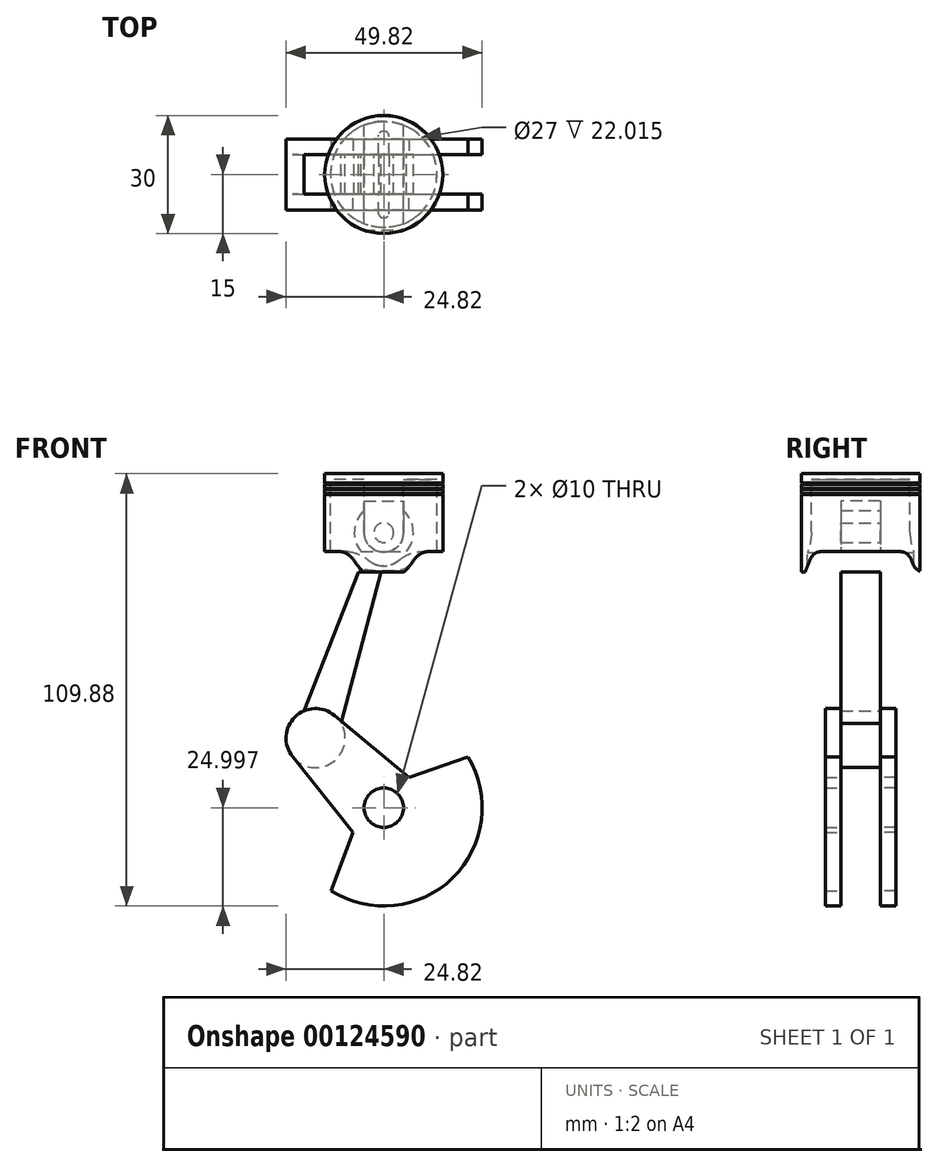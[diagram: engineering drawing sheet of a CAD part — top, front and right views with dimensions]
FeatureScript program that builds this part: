
annotation { "Feature Type Name" : "Feature", "Feature Type Description" : "" }
export const myFeature = defineFeature(function(context is Context, id is Id, definition is map)
    precondition{}
    {
        {
            var Q0;
            Q0=qCreatedBy(makeId("Front.planeOp"),FACE);
            var sketch = newSketch(context, id + "F0", { "sketchPlane" : qUnion([Q0])});
            skLineSegment(sketch, "E0", {"start": v(-89.18, 0) * mm, "end": v(136.85, 0) * mm, "construction": true});
            skLineSegment(sketch, "E1", {"start": v(-89.18, 90) * mm, "end": v(136.85, 90) * mm, "construction": true});
            skLineSegment(sketch, "E2", {"start": v(0, -43.94) * mm, "end": v(0, 141.42) * mm, "construction": true});
            skLineSegment(sketch, "E3", {"start": v(-89.18, 50) * mm, "end": v(92.22, 50) * mm, "construction": true});
            skLineSegment(sketch, "E4", {"start": v(0, 0) * mm, "end": v(-17.32, 10) * mm});
            skLineSegment(sketch, "E5.bottom", {"start": v(-15, 77.2) * mm, "end": v(15, 77.2) * mm});
            skLineSegment(sketch, "E5.top", {"start": v(-15, 52.2) * mm, "end": v(15, 52.2) * mm});
            skLineSegment(sketch, "E5.left", {"start": v(-15, 77.2) * mm, "end": v(-15, 52.2) * mm});
            skLineSegment(sketch, "E5.right", {"start": v(15, 77.2) * mm, "end": v(15, 52.2) * mm});
            skCircle(sketch, "E6", {"center": v(0, 62.2) * mm, "radius": 2.5 * mm});
            skLineSegment(sketch, "E7", {"start": v(-5, 77.2) * mm, "end": v(-5, 62.2) * mm});
            skLineSegment(sketch, "E8", {"start": v(5, 77.2) * mm, "end": v(5, 62.2) * mm});
            skArc(sketch, "E9", {"start": v(-5, 62.2) * mm, "mid": v(0, 57.2) * mm, "end": v(5, 62.2) * mm});
            skLineSegment(sketch, "E10", {"start": v(-5, 70.2) * mm, "end": v(5, 70.2) * mm});
            skLineSegment(sketch, "E11", {"start": v(0, 62.2) * mm, "end": v(-17.32, 10) * mm});
            skSolve(sketch);
        }
        {
            var Q0;
            Q0=qCreatedBy(makeId("Front.planeOp"),FACE);
            var sketch = newSketch(context, id + "F1", { "sketchPlane" : qUnion([Q0])});
            skLineSegment(sketch, "E12.0", {"start": v(0, 77.2) * mm, "end": v(15, 77.2) * mm});
            skLineSegment(sketch, "E12.1", {"start": v(15, 77.2) * mm, "end": v(15, 52.2) * mm});
            skLineSegment(sketch, "E12.2", {"start": v(0, 52.2) * mm, "end": v(15, 52.2) * mm});
            skLineSegment(sketch, "E13", {"start": v(0, 77.2) * mm, "end": v(0, 52.2) * mm});
            skPoint(sketch, "E14.orphan", {"position": v(-15, 77.2) * mm});
            skPoint(sketch, "E15.orphan", {"position": v(-15, 52.2) * mm});
            skSolve(sketch);
        }
        {
            var Q0;
            Q0=makeQuery(id+"F1.imprint","IMPRINT",FACE,{"disambiguationData":[TD([[makeQuery(id+"F1.imprint","IMPRINT",EDGE,{"derivedFrom":sQuery(id+"F1.wireOp",EDGE,"E12.0")}),-1.0]])]});
            var Q1;
            Q1=sQuery(id+"F1.wireOp",EDGE,"E13");
            revolve(context, id + "F2", {"entities" : qUnion([Q0]), "axis" : qUnion([Q1]), "revolveType" : RevolveType.FULL});
        }
        {
            var Q0;
            Q0=makeQuery(id+"F2.opRevolve","SWEPT_FACE",FACE,{"disambiguationData":[OSD([sQuery(id+"F1.wireOp",EDGE,"E12.2")])]});
            shell(context, id + "F3", {"entities" : qUnion([Q0]), "thickness" : 1.5 * mm});
        }
        {
            var Q0;
            {var subQ5=sQuery(id+"F0.wireOp",EDGE,"E10");Q0=makeQuery(id+"F0.imprint","IMPRINT",FACE,{"disambiguationData":[TD([[makeQuery(id+"F0.imprint","IMPRINT",EDGE,{"derivedFrom":subQ5}),1.0]])]});}
            var Q1;
            Q1=makeQuery(id+"F0.imprint","IMPRINT",FACE,{"disambiguationData":[TD([[makeQuery(id+"F0.imprint","IMPRINT",EDGE,{"derivedFrom":sQuery(id+"F0.wireOp",EDGE,"E6")}),-1.0]])]});
            var Q2;
            Q2=makeQuery(id+"F2.opRevolve","SWEPT_FACE",FACE,{"disambiguationData":[OSD([sQuery(id+"F1.wireOp",EDGE,"E12.1")])]});
            var Q3;
            Q3=makeQuery(id+"F3.opShell","OFFSET_FACE",FACE,{"disambiguationData":[OSD([sQuery(id+"F1.wireOp",EDGE,"E12.1")])]});
            extrude(context, id + "F4", {"entities" : qUnion([Q0, Q1]), "operationType" : NewBodyOperationType.ADD, "endBound" : BoundingType.UP_TO_SURFACE, "endBoundEntityFace" : qUnion([Q2]), "depth" : 25 * mm, "hasSecondDirection" : true, "secondDirectionBound" : SecondDirectionBoundingType.UP_TO_SURFACE, "secondDirectionOppositeDirection" : true, "secondDirectionBoundEntityFace" : qUnion([Q3]), "secondDirectionDepth" : 25 * mm});
        }
        {
            var Q0;
            Q0=qCreatedBy(makeId("Front.planeOp"),FACE);
            var sketch = newSketch(context, id + "F5", { "sketchPlane" : qUnion([Q0])});
            skCircle(sketch, "E16", {"center": v(0, 62.2) * mm, "radius": 7.5 * mm});
            skCircle(sketch, "E17", {"center": v(-17.32, 10) * mm, "radius": 4 * mm});
            skCircle(sketch, "E18", {"center": v(-17.32, 10) * mm, "radius": 7.5 * mm});
            skLineSegment(sketch, "E19", {"start": v(0, 54.7) * mm, "end": v(-10.81, 13.73) * mm});
            skLineSegment(sketch, "E20", {"start": v(-4.71, 56.37) * mm, "end": v(-20.3, 16.88) * mm});
            skCircle(sketch, "E21", {"center": v(0, 62.2) * mm, "radius": 2.5 * mm});
            skSolve(sketch);
        }
        {
            var Q0;
            Q0 = qSketchRegion(id + "F5", true);
            extrude(context, id + "F6", {"entities" : qUnion([Q0]), "endBound" : BoundingType.SYMMETRIC, "depth" : 10 * mm});
        }
        {
            var Q0;
            Q0=makeQuery(id+"F6.opExtrude","CAP_FACE",FACE,{"disambiguationData":[OSD([sQuery(id+"F5.wireOp",EDGE,"E16"),sQuery(id+"F5.wireOp",EDGE,"E17"),sQuery(id+"F5.wireOp",EDGE,"E18"),sQuery(id+"F5.wireOp",EDGE,"E19"),sQuery(id+"F5.wireOp",EDGE,"E20"),sQuery(id+"F5.wireOp",EDGE,"E21")])],"isStart":false});
            var sketch = newSketch(context, id + "F7", { "sketchPlane" : qUnion([Q0])});
            skCircle(sketch, "E22.0", {"center": v(-17.32, 10) * mm, "radius": 7.5 * mm});
            skPoint(sketch, "E22.1", {"position": v(-17.32, 10) * mm});
            skCircle(sketch, "E23", {"center": v(0, -7.68) * mm, "radius": 5 * mm});
            skCircle(sketch, "E24", {"center": v(0, -7.68) * mm, "radius": 10 * mm});
            skLineSegment(sketch, "E25", {"start": v(-7.81, -13.92) * mm, "end": v(-23.18, 5.32) * mm});
            skLineSegment(sketch, "E26", {"start": v(-12.52, 15.76) * mm, "end": v(6.4, 0) * mm});
            skLineSegment(sketch, "E27", {"start": v(-7.81, -13.92) * mm, "end": v(0, -7.68) * mm, "construction": true});
            skLineSegment(sketch, "E28", {"start": v(0, -7.68) * mm, "end": v(6.4, 0) * mm, "construction": true});
            skLineSegment(sketch, "E29", {"start": v(0, -7.68) * mm, "end": v(19.26, -27.34) * mm, "construction": true});
            skLineSegment(sketch, "E30", {"start": v(6.4, 0) * mm, "end": v(21.38, 5.28) * mm});
            skLineSegment(sketch, "E31", {"start": v(-7.81, -13.92) * mm, "end": v(-13.4, -28.79) * mm});
            skArc(sketch, "E32", {"start": v(-13.4, -28.79) * mm, "mid": v(17.5, -25.54) * mm, "end": v(21.38, 5.28) * mm});
            skCircle(sketch, "E33.1", {"center": v(-17.32, 10) * mm, "radius": 4 * mm});
            skSolve(sketch);
        }
        {
            var Q0;
            Q0=makeQuery(id+"F5.imprint","IMPRINT",FACE,{"disambiguationData":[TD([[makeQuery(id+"F5.imprint","IMPRINT",EDGE,{"derivedFrom":sQuery(id+"F5.wireOp",EDGE,"E21")}),1.0]])]});
            var Q1;
            Q1=makeQuery(id+"F0.imprint","IMPRINT",FACE,{"disambiguationData":[TD([[makeQuery(id+"F0.imprint","IMPRINT",EDGE,{"derivedFrom":sQuery(id+"F0.wireOp",EDGE,"E6")}),-1.0]])]});
            extrude(context, id + "F8", {"entities" : qUnion([Q0, Q1]), "operationType" : NewBodyOperationType.REMOVE, "endBound" : BoundingType.SYMMETRIC, "oppositeDirection" : true, "depth" : 10 * mm});
        }
        {
            var Q0;
            Q0=qCreatedBy(makeId("Right.planeOp"),FACE);
            var sketch = newSketch(context, id + "F9", { "sketchPlane" : qUnion([Q0])});
            skLineSegment(sketch, "E34", {"start": v(-14.08, 52.2) * mm, "end": v(-12.07, 57.37) * mm});
            skLineSegment(sketch, "E35", {"start": v(-12.07, 57.37) * mm, "end": v(12.07, 57.37) * mm});
            skLineSegment(sketch, "E36", {"start": v(12.07, 57.37) * mm, "end": v(14.08, 52.2) * mm});
            skLineSegment(sketch, "E37", {"start": v(0, -1.25) * mm, "end": v(0, 76.4) * mm, "construction": true});
            skLineSegment(sketch, "E38", {"start": v(-14.08, 52.2) * mm, "end": v(14.08, 52.2) * mm});
            skLineSegment(sketch, "E39.0", {"start": v(-15, 52.2) * mm, "end": v(15, 52.2) * mm});
            skSolve(sketch);
        }
        {
            var Q0;
            Q0 = qSketchRegion(id + "F7", true);
            var Q1;
            Q1=makeQuery(id+"F7.imprint","IMPRINT",FACE,{"disambiguationData":[TD([[makeQuery(id+"F7.imprint","IMPRINT",EDGE,{"derivedFrom":sQuery(id+"F7.wireOp",EDGE,"E33.1")}),1.0]])]});
            extrude(context, id + "F10", {"entities" : qUnion([Q0, Q1]), "depth" : 4 * mm});
        }
        {
            var Q0;
            Q0=makeQuery(id+"F10.opExtrude","SWEPT_BODY",BODY,{"disambiguationData":[OSD([sQuery(id+"F7.wireOp",EDGE,"E22.0"),sQuery(id+"F7.wireOp",EDGE,"E23"),sQuery(id+"F7.wireOp",EDGE,"E25"),sQuery(id+"F7.wireOp",EDGE,"E26"),sQuery(id+"F7.wireOp",EDGE,"E30"),sQuery(id+"F7.wireOp",EDGE,"E31"),sQuery(id+"F7.wireOp",EDGE,"E32")])]});
            var Q1;
            Q1=qCreatedBy(makeId("Front.planeOp"),FACE);
            mirror(context, id + "F11", {"entities" : qUnion([Q0]), "mirrorPlane" : qUnion([Q1])});
        }
        {
            var Q0;
            {var subQ0=sQuery(id+"F9.wireOp",EDGE,"E34");Q0=makeQuery(id+"F9.imprint","IMPRINT",FACE,{"disambiguationData":[TD([[makeQuery(id+"F9.imprint","IMPRINT",EDGE,{"derivedFrom":subQ0}),-1.0]])]});}
            extrude(context, id + "F12", {"entities" : qUnion([Q0]), "operationType" : NewBodyOperationType.REMOVE, "endBound" : BoundingType.THROUGH_ALL, "oppositeDirection" : true, "depth" : 25 * mm, "hasSecondDirection" : true, "secondDirectionBound" : SecondDirectionBoundingType.THROUGH_ALL, "secondDirectionOppositeDirection" : false, "secondDirectionDepth" : 25 * mm});
        }
        {
            var Q0;
            Q0=makeQuery(id+"F7.imprint","IMPRINT",FACE,{"disambiguationData":[TD([[makeQuery(id+"F7.imprint","IMPRINT",EDGE,{"derivedFrom":sQuery(id+"F7.wireOp",EDGE,"E33.1")}),1.0]])]});
            extrude(context, id + "F13", {"entities" : qUnion([Q0]), "operationType" : NewBodyOperationType.ADD, "oppositeDirection" : true, "depth" : 10 * mm});
        }
        {
            var Q0;
            Q0=qCreatedBy(makeId("Front.planeOp"),FACE);
            var sketch = newSketch(context, id + "F14", { "sketchPlane" : qUnion([Q0])});
            skLineSegment(sketch, "E40", {"start": v(0, 0) * mm, "end": v(0, 77.2) * mm, "construction": true});
            skLineSegment(sketch, "E41", {"start": v(0, 77.2) * mm, "end": v(15, 77.2) * mm, "construction": true});
            skLineSegment(sketch, "E42", {"start": v(15, 77.2) * mm, "end": v(15, 75.9) * mm, "construction": true});
            skLineSegment(sketch, "E43", {"start": v(15, 75.9) * mm, "end": v(15, 74.6) * mm, "construction": true});
            skLineSegment(sketch, "E44", {"start": v(15, 74.6) * mm, "end": v(15, 73.3) * mm, "construction": true});
            skLineSegment(sketch, "E45", {"start": v(15, 73.3) * mm, "end": v(15, 72) * mm, "construction": true});
            skCircle(sketch, "E46", {"center": v(15, 74.6) * mm, "radius": 0.15 * mm});
            skCircle(sketch, "E47", {"center": v(15, 73.3) * mm, "radius": 0.15 * mm});
            skCircle(sketch, "E48", {"center": v(15, 72) * mm, "radius": 0.15 * mm});
            skSolve(sketch);
        }
        {
            var Q0;
            Q0 = qSketchRegion(id + "F14", true);
            var Q1;
            Q1=makeQuery(id+"F2.opRevolve","SWEPT_EDGE",EDGE,{"disambiguationData":[OSD([sQuery(id+"F1.wireOp",EDGE,"E12.0"),sQuery(id+"F1.wireOp",EDGE,"E12.1")])]});
            revolve(context, id + "F15", {"operationType" : NewBodyOperationType.REMOVE, "entities" : qUnion([Q0]), "axis" : qUnion([Q1]), "revolveType" : RevolveType.FULL, "oppositeDirection" : true});
        }
        {
            var Q0;
            {var subQ0=sQuery(id+"F1.wireOp",EDGE,"E12.1");var subQ1=sQuery(id+"F9.wireOp",EDGE,"E34");var subQ2=sQuery(id+"F9.wireOp",EDGE,"E35");Q0=makeQuery(id+"F12.boolean.opBoolean","COPY",EDGE,{"disambiguationData":[TD([makeQuery(id+"F2.opRevolve","SWEPT_FACE",FACE,{"disambiguationData":[OSD([subQ0])]}),makeQuery(id+"F3.opShell","OFFSET_FACE",FACE,{"disambiguationData":[OSD([subQ0])]}),makeQuery(id+"F12.opExtrude","SWEPT_FACE",FACE,{"disambiguationData":[OSD([subQ1])]}),makeQuery(id+"F12.opExtrude","SWEPT_FACE",FACE,{"disambiguationData":[OSD([subQ2])]})]),OD(1.0)],"derivedFrom":makeQuery(id+"F12.opExtrude","SWEPT_EDGE",EDGE,{"disambiguationData":[OSD([subQ1,subQ2])]})});}
            var Q1;
            {var subQ0=sQuery(id+"F1.wireOp",EDGE,"E12.1");var subQ1=sQuery(id+"F9.wireOp",EDGE,"E35");var subQ2=sQuery(id+"F9.wireOp",EDGE,"E36");Q1=makeQuery(id+"F12.boolean.opBoolean","COPY",EDGE,{"disambiguationData":[TD([makeQuery(id+"F2.opRevolve","SWEPT_FACE",FACE,{"disambiguationData":[OSD([subQ0])]}),makeQuery(id+"F3.opShell","OFFSET_FACE",FACE,{"disambiguationData":[OSD([subQ0])]}),makeQuery(id+"F12.opExtrude","SWEPT_FACE",FACE,{"disambiguationData":[OSD([subQ1])]}),makeQuery(id+"F12.opExtrude","SWEPT_FACE",FACE,{"disambiguationData":[OSD([subQ2])]})]),OD(1.0)],"derivedFrom":makeQuery(id+"F12.opExtrude","SWEPT_EDGE",EDGE,{"disambiguationData":[OSD([subQ1,subQ2])]})});}
            var Q2;
            {var subQ0=sQuery(id+"F1.wireOp",EDGE,"E12.1");var subQ1=sQuery(id+"F9.wireOp",EDGE,"E35");var subQ2=sQuery(id+"F9.wireOp",EDGE,"E36");Q2=makeQuery(id+"F12.boolean.opBoolean","COPY",EDGE,{"disambiguationData":[TD([makeQuery(id+"F2.opRevolve","SWEPT_FACE",FACE,{"disambiguationData":[OSD([subQ0])]}),makeQuery(id+"F3.opShell","OFFSET_FACE",FACE,{"disambiguationData":[OSD([subQ0])]}),makeQuery(id+"F12.opExtrude","SWEPT_FACE",FACE,{"disambiguationData":[OSD([subQ1])]}),makeQuery(id+"F12.opExtrude","SWEPT_FACE",FACE,{"disambiguationData":[OSD([subQ2])]})]),OD(0.0)],"derivedFrom":makeQuery(id+"F12.opExtrude","SWEPT_EDGE",EDGE,{"disambiguationData":[OSD([subQ1,subQ2])]})});}
            var Q3;
            {var subQ0=sQuery(id+"F1.wireOp",EDGE,"E12.1");var subQ1=sQuery(id+"F9.wireOp",EDGE,"E34");var subQ2=sQuery(id+"F9.wireOp",EDGE,"E35");Q3=makeQuery(id+"F12.boolean.opBoolean","COPY",EDGE,{"disambiguationData":[TD([makeQuery(id+"F2.opRevolve","SWEPT_FACE",FACE,{"disambiguationData":[OSD([subQ0])]}),makeQuery(id+"F3.opShell","OFFSET_FACE",FACE,{"disambiguationData":[OSD([subQ0])]}),makeQuery(id+"F12.opExtrude","SWEPT_FACE",FACE,{"disambiguationData":[OSD([subQ1])]}),makeQuery(id+"F12.opExtrude","SWEPT_FACE",FACE,{"disambiguationData":[OSD([subQ2])]})]),OD(0.0)],"derivedFrom":makeQuery(id+"F12.opExtrude","SWEPT_EDGE",EDGE,{"disambiguationData":[OSD([subQ1,subQ2])]})});}
            fillet(context, id + "F16", {"entities" : qUnion([Q0, Q1, Q2, Q3]), "radius" : 3 * mm, "tangentPropagation" : true, "allowEdgeOverflow" : false});
        }
        {
            var Q0;
            Q0=makeQuery(id+"F12.boolean.opBoolean","COPY",EDGE,{"derivedFrom":makeQuery(id+"F12.opExtrude","SWEPT_EDGE",EDGE,{"disambiguationData":[OSD([sQuery(id+"F9.wireOp",EDGE,"E34"),sQuery(id+"F9.wireOp",EDGE,"E39.0")])]})});
            var Q1;
            Q1=makeQuery(id+"F12.boolean.opBoolean","COPY",EDGE,{"derivedFrom":makeQuery(id+"F12.opExtrude","SWEPT_EDGE",EDGE,{"disambiguationData":[OSD([sQuery(id+"F9.wireOp",EDGE,"E36"),sQuery(id+"F9.wireOp",EDGE,"E39.0")])]})});
            fillet(context, id + "F17", {"entities" : qUnion([Q0, Q1]), "radius" : 3 * mm, "tangentPropagation" : true, "allowEdgeOverflow" : false});
        }
        {
            var Q0;
            Q0=makeQuery(id+"F5.imprint","IMPRINT",FACE,{"disambiguationData":[TD([[makeQuery(id+"F5.imprint","IMPRINT",EDGE,{"derivedFrom":sQuery(id+"F5.wireOp",EDGE,"E21")}),1.0]])]});
            var Q1;
            Q1=makeQuery(id+"F4.boolean.opBoolean","SPLIT",FACE,{"disambiguationData":[TD([makeQuery(id+"F2.opRevolve","SWEPT_FACE",FACE,{"disambiguationData":[OSD([sQuery(id+"F1.wireOp",EDGE,"E12.2")])]}),makeQuery(id+"F3.opShell","OFFSET_FACE",FACE,{"disambiguationData":[OSD([sQuery(id+"F1.wireOp",EDGE,"E12.0")])]}),makeQuery(id+"F4.opExtrude","SWEPT_FACE",FACE,{"disambiguationData":[OSD([sQuery(id+"F0.wireOp",EDGE,"E7")])]}),makeQuery(id+"F4.opExtrude","SWEPT_FACE",FACE,{"disambiguationData":[OSD([sQuery(id+"F0.wireOp",EDGE,"E8")])]}),makeQuery(id+"F4.opExtrude","SWEPT_FACE",FACE,{"disambiguationData":[OSD([sQuery(id+"F0.wireOp",EDGE,"E9")])]})])],"derivedFrom":makeQuery(id+"F3.opShell","OFFSET_FACE",FACE,{"disambiguationData":[OSD([sQuery(id+"F1.wireOp",EDGE,"E12.1")])]})});
            var Q2;
            Q2=makeQuery(id+"F4.boolean.opBoolean","SPLIT",FACE,{"disambiguationData":[TD([makeQuery(id+"F2.opRevolve","SWEPT_FACE",FACE,{"disambiguationData":[OSD([sQuery(id+"F1.wireOp",EDGE,"E12.2")])]}),makeQuery(id+"F3.opShell","OFFSET_FACE",FACE,{"disambiguationData":[OSD([sQuery(id+"F1.wireOp",EDGE,"E12.0")])]}),makeQuery(id+"F4.opExtrude","SWEPT_FACE",FACE,{"disambiguationData":[OSD([sQuery(id+"F0.wireOp",EDGE,"E7")])]}),makeQuery(id+"F4.opExtrude","SWEPT_FACE",FACE,{"disambiguationData":[OSD([sQuery(id+"F0.wireOp",EDGE,"E8")])]}),makeQuery(id+"F4.opExtrude","SWEPT_FACE",FACE,{"disambiguationData":[OSD([sQuery(id+"F0.wireOp",EDGE,"E9")])]})])],"derivedFrom":makeQuery(id+"F3.opShell","OFFSET_FACE",FACE,{"disambiguationData":[OSD([sQuery(id+"F1.wireOp",EDGE,"E12.1")])]})});
            extrude(context, id + "F18", {"entities" : qUnion([Q0]), "operationType" : NewBodyOperationType.ADD, "endBound" : BoundingType.UP_TO_SURFACE, "endBoundEntityFace" : qUnion([Q1]), "depth" : 25 * mm, "hasSecondDirection" : true, "secondDirectionBound" : SecondDirectionBoundingType.UP_TO_SURFACE, "secondDirectionOppositeDirection" : true, "secondDirectionBoundEntityFace" : qUnion([Q2]), "secondDirectionDepth" : 25 * mm});
        }
    });
